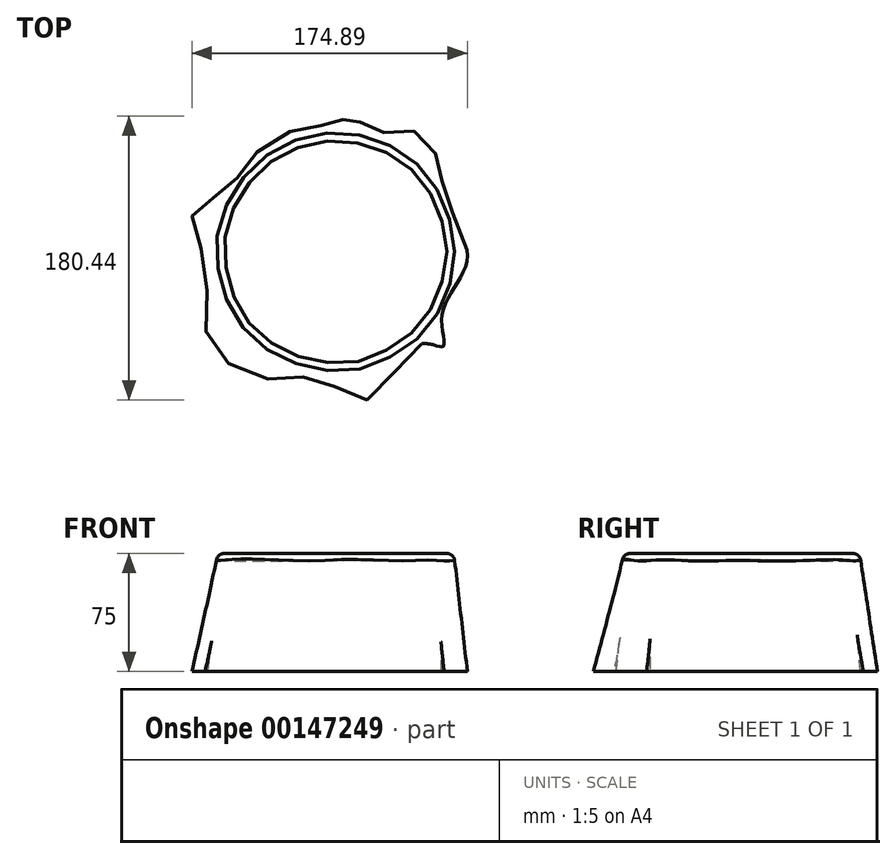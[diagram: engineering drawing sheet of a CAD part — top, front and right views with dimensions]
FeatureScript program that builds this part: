
annotation { "Feature Type Name" : "Feature", "Feature Type Description" : "" }
export const myFeature = defineFeature(function(context is Context, id is Id, definition is map)
    precondition{}
    {
        {
            var Q0;
            Q0=qCreatedBy(makeId("Top.planeOp"),FACE);
            var sketch = newSketch(context, id + "F0", { "sketchPlane" : qUnion([Q0])});
            skCircle(sketch, "E0", {"center": v(0, 0) * mm, "radius": 75 * mm});
            skSolve(sketch);
        }
        {
            var Q0;
            Q0=qCreatedBy(makeId("Top.planeOp"),FACE);
            cPlane(context, id + "F1", {"entities" : qUnion([Q0]), "cplaneType" : CPlaneType.OFFSET, "offset" : 75 * mm, "oppositeDirection" : true, "width" : 150 * mm, "height" : 150 * mm});
        }
        {
            var Q0;
            Q0=qCreatedBy(id+"F1.planeOp",FACE);
            var sketch = newSketch(context, id + "F2", { "sketchPlane" : qUnion([Q0])});
            skFitSpline(sketch, "E1", {"points": [v(0, 81.23) * mm, v(9.97, 86.12) * mm, v(23.75, 76.02) * mm, v(47.94, 76.94) * mm, v(65.4, 57.34) * mm, v(69.38, 35.3) * mm, v(83.47, -4.21) * mm, v(67.54, -39.73) * mm, v(68.16, -60.25) * mm, v(52.84, -59.02) * mm, v(21.6, -93.63) * mm, v(-9.62, -81.07) * mm, v(-40.55, -81.07) * mm, v(-80.36, -57.8) * mm, v(-82.2, -10.34) * mm, v(-90.77, 24.27) * mm, v(-70.26, 38.66) * mm, v(-52.8, 60.4) * mm, v(-19.12, 79.39) * mm, v(0, 81.23) * mm]});
            skSolve(sketch);
        }
        {
            var Q0;
            Q0=makeQuery(id+"F0.imprint","IMPRINT",FACE,{"disambiguationData":[TD([[makeQuery(id+"F0.imprint","IMPRINT",EDGE,{"derivedFrom":sQuery(id+"F0.wireOp",EDGE,"E0")}),1.0]])]});
            var Q1;
            Q1=makeQuery(id+"F2.imprint","IMPRINT",FACE,{"disambiguationData":[TD([[makeQuery(id+"F2.imprint","IMPRINT",EDGE,{"derivedFrom":sQuery(id+"F2.wireOp",EDGE,"E1")}),-1.0]])]});
            loft(context, id + "F3", {"sheetProfilesArray" : [{ "sheetProfileEntities" : qUnion([Q0]) }, { "sheetProfileEntities" : qUnion([Q1]) }]});
        }
        {
            var Q0;
            Q0=makeQuery(id+"F3.opLoft","MID_CAP_EDGE",EDGE,{"disambiguationData":[OSD([sQuery(id+"F0.wireOp",EDGE,"E0")])],"capPos":0.0});
            fillet(context, id + "F4", {"entities" : qUnion([Q0]), "radius" : 5 * mm, "tangentPropagation" : true, "allowEdgeOverflow" : false});
        }
    });
